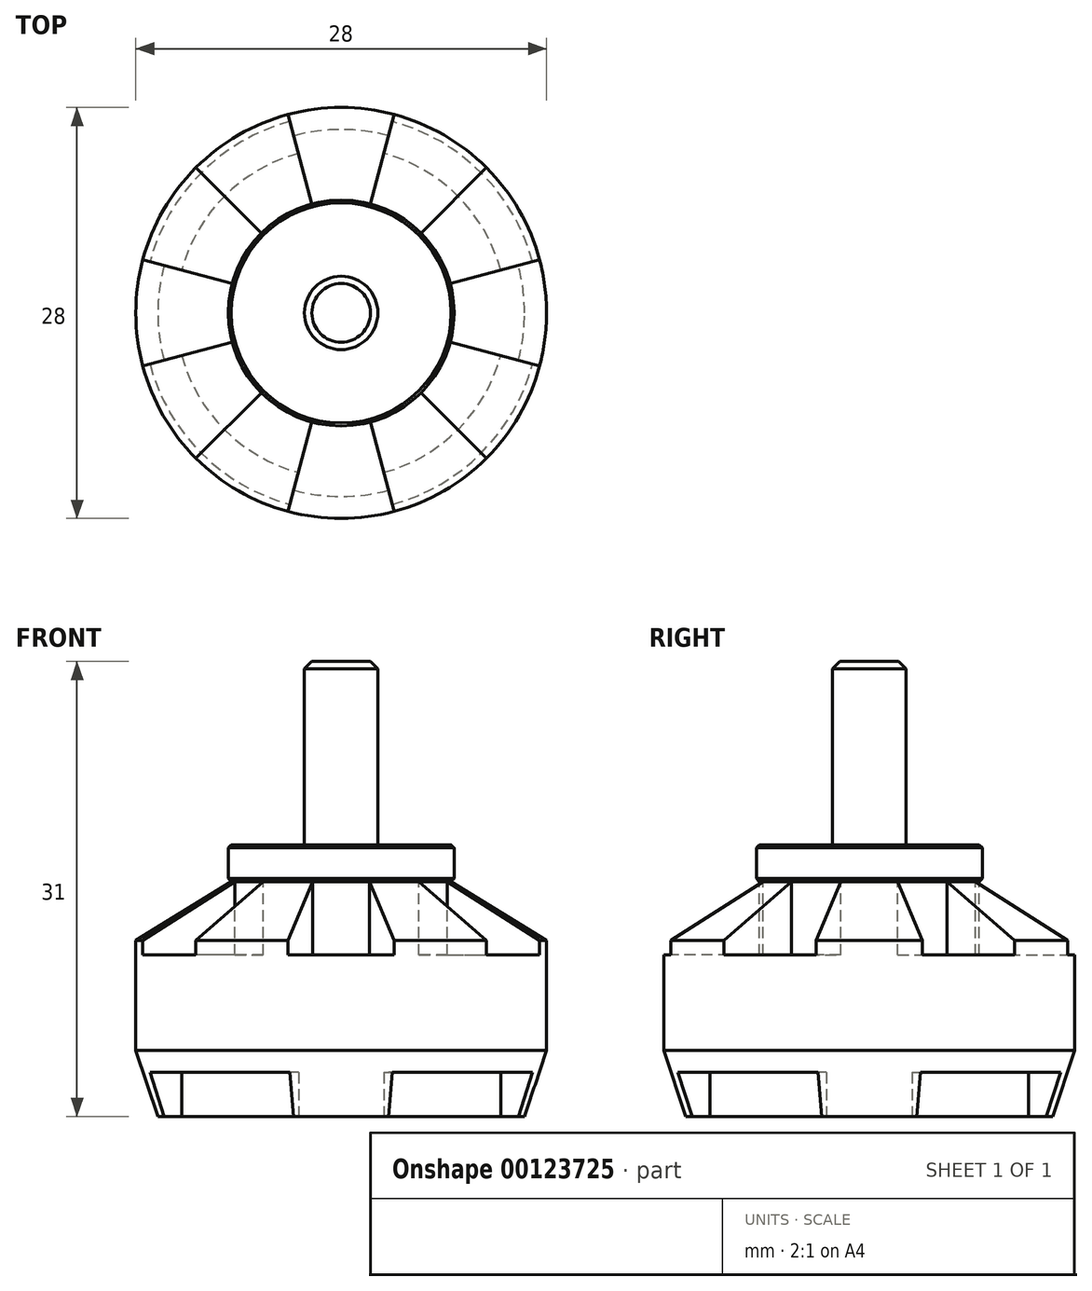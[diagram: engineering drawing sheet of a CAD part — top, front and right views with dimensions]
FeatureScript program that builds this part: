
annotation { "Feature Type Name" : "Feature", "Feature Type Description" : "" }
export const myFeature = defineFeature(function(context is Context, id is Id, definition is map)
    precondition{}
    {
        {
            var Q0;
            Q0=qCreatedBy(makeId("Front.planeOp"),FACE);
            var sketch = newSketch(context, id + "F0", { "sketchPlane" : qUnion([Q0])});
            skLineSegment(sketch, "E0.top", {"start": v(0, 0) * mm, "end": v(12.5, 0) * mm});
            skLineSegment(sketch, "E0.right", {"start": v(14, 12) * mm, "end": v(14, 4.5) * mm});
            skLineSegment(sketch, "E1", {"start": v(0, 16) * mm, "end": v(7.5, 16) * mm});
            skLineSegment(sketch, "E2", {"start": v(7.5, 16) * mm, "end": v(14, 12) * mm});
            skLineSegment(sketch, "E3", {"start": v(0, 16) * mm, "end": v(0, 0) * mm});
            skLineSegment(sketch, "E4", {"start": v(12.5, 0) * mm, "end": v(14, 4.5) * mm});
            skPoint(sketch, "E5.orphan", {"position": v(14, 0) * mm});
            skSolve(sketch);
        }
        {
            var Q0;
            Q0=qSketchRegion(id+"F0",true);
            var Q1;
            Q1=sQuery(id+"F0.wireOp",EDGE,"E3");
            revolve(context, id + "F1", {"entities" : qUnion([Q0]), "axis" : qUnion([Q1]), "revolveType" : RevolveType.FULL});
        }
        {
            var Q0;
            Q0=makeQuery(id+"F1.opRevolve","SWEPT_FACE",FACE,{"disambiguationData":[OSD([sQuery(id+"F0.wireOp",EDGE,"E1")])]});
            var sketch = newSketch(context, id + "F2", { "sketchPlane" : qUnion([Q0])});
            skArc(sketch, "E6", {"start": v(1.94, 7.24) * mm, "mid": v(0, 7.5) * mm, "end": v(-1.94, 7.24) * mm});
            skArc(sketch, "E7", {"start": v(3.62, 13.52) * mm, "mid": v(0, 14) * mm, "end": v(-3.62, 13.52) * mm});
            skLineSegment(sketch, "E8", {"start": v(0, 0) * mm, "end": v(-1.94, 7.24) * mm, "construction": true});
            skLineSegment(sketch, "E9", {"start": v(-1.94, 7.24) * mm, "end": v(-3.62, 13.52) * mm});
            skLineSegment(sketch, "E10", {"start": v(0, 0) * mm, "end": v(1.94, 7.24) * mm, "construction": true});
            skLineSegment(sketch, "E11", {"start": v(1.94, 7.24) * mm, "end": v(3.62, 13.52) * mm});
            skArc(sketch, "E12.1.0", {"start": v(-5.3, 5.3) * mm, "mid": v(-6.5, 3.75) * mm, "end": v(-7.24, 1.94) * mm});
            skArc(sketch, "E12.1.1", {"start": v(-9.9, 9.9) * mm, "mid": v(-12.12, 7) * mm, "end": v(-13.52, 3.62) * mm});
            skLineSegment(sketch, "E12.1.2", {"start": v(-5.3, 5.3) * mm, "end": v(-9.9, 9.9) * mm});
            skLineSegment(sketch, "E12.1.3", {"start": v(-7.24, 1.94) * mm, "end": v(-13.52, 3.62) * mm});
            skArc(sketch, "E12.2.0", {"start": v(-7.24, -1.94) * mm, "mid": v(-6.5, -3.75) * mm, "end": v(-5.3, -5.3) * mm});
            skArc(sketch, "E12.2.1", {"start": v(-13.52, -3.62) * mm, "mid": v(-12.12, -7) * mm, "end": v(-9.9, -9.9) * mm});
            skLineSegment(sketch, "E12.2.2", {"start": v(-7.24, -1.94) * mm, "end": v(-13.52, -3.62) * mm});
            skLineSegment(sketch, "E12.2.3", {"start": v(-5.3, -5.3) * mm, "end": v(-9.9, -9.9) * mm});
            skArc(sketch, "E12.3.0", {"start": v(-1.94, -7.24) * mm, "mid": v(0, -7.5) * mm, "end": v(1.94, -7.24) * mm});
            skArc(sketch, "E12.3.1", {"start": v(-3.62, -13.52) * mm, "mid": v(0, -14) * mm, "end": v(3.62, -13.52) * mm});
            skLineSegment(sketch, "E12.3.2", {"start": v(-1.94, -7.24) * mm, "end": v(-3.62, -13.52) * mm});
            skLineSegment(sketch, "E12.3.3", {"start": v(1.94, -7.24) * mm, "end": v(3.62, -13.52) * mm});
            skArc(sketch, "E12.4.0", {"start": v(5.3, -5.3) * mm, "mid": v(6.5, -3.75) * mm, "end": v(7.24, -1.94) * mm});
            skArc(sketch, "E12.4.1", {"start": v(9.9, -9.9) * mm, "mid": v(12.12, -7) * mm, "end": v(13.52, -3.62) * mm});
            skLineSegment(sketch, "E12.4.2", {"start": v(5.3, -5.3) * mm, "end": v(9.9, -9.9) * mm});
            skLineSegment(sketch, "E12.4.3", {"start": v(7.24, -1.94) * mm, "end": v(13.52, -3.62) * mm});
            skArc(sketch, "E12.5.0", {"start": v(7.24, 1.94) * mm, "mid": v(6.5, 3.75) * mm, "end": v(5.3, 5.3) * mm});
            skArc(sketch, "E12.5.1", {"start": v(13.52, 3.62) * mm, "mid": v(12.12, 7) * mm, "end": v(9.9, 9.9) * mm});
            skLineSegment(sketch, "E12.5.2", {"start": v(7.24, 1.94) * mm, "end": v(13.52, 3.62) * mm});
            skLineSegment(sketch, "E12.5.3", {"start": v(5.3, 5.3) * mm, "end": v(9.9, 9.9) * mm});
            skSolve(sketch);
        }
        {
            var Q0;
            Q0=qSketchRegion(id+"F2",true);
            extrude(context, id + "F3", {"entities" : qUnion([Q0]), "operationType" : NewBodyOperationType.REMOVE, "oppositeDirection" : true, "depth" : 5 * mm});
        }
        {
            var Q0;
            Q0=makeQuery(id+"F1.opRevolve","SWEPT_FACE",FACE,{"disambiguationData":[OSD([sQuery(id+"F0.wireOp",EDGE,"E0.top")])]});
            var sketch = newSketch(context, id + "F4", { "sketchPlane" : qUnion([Q0])});
            skArc(sketch, "E13", {"start": v(10.87, 2.91) * mm, "mid": v(7.95, 7.95) * mm, "end": v(2.91, 10.87) * mm});
            skArc(sketch, "E14", {"start": v(13.52, 3.62) * mm, "mid": v(9.9, 9.9) * mm, "end": v(3.62, 13.52) * mm});
            skLineSegment(sketch, "E15", {"start": v(0, 0) * mm, "end": v(2.91, 10.87) * mm, "construction": true});
            skLineSegment(sketch, "E16", {"start": v(2.91, 10.87) * mm, "end": v(3.62, 13.52) * mm});
            skLineSegment(sketch, "E17", {"start": v(0, 0) * mm, "end": v(10.87, 2.91) * mm, "construction": true});
            skLineSegment(sketch, "E18", {"start": v(10.87, 2.91) * mm, "end": v(13.52, 3.62) * mm});
            skArc(sketch, "E19.1.0", {"start": v(-3.62, 13.52) * mm, "mid": v(-9.9, 9.9) * mm, "end": v(-13.52, 3.62) * mm});
            skArc(sketch, "E19.1.1", {"start": v(-2.91, 10.87) * mm, "mid": v(-7.95, 7.95) * mm, "end": v(-10.87, 2.91) * mm});
            skLineSegment(sketch, "E19.1.2", {"start": v(-10.87, 2.91) * mm, "end": v(-13.52, 3.62) * mm});
            skLineSegment(sketch, "E19.1.3", {"start": v(-2.91, 10.87) * mm, "end": v(-3.62, 13.52) * mm});
            skArc(sketch, "E19.2.0", {"start": v(-13.52, -3.62) * mm, "mid": v(-9.9, -9.9) * mm, "end": v(-3.62, -13.52) * mm});
            skArc(sketch, "E19.2.1", {"start": v(-10.87, -2.91) * mm, "mid": v(-7.95, -7.95) * mm, "end": v(-2.91, -10.87) * mm});
            skLineSegment(sketch, "E19.2.2", {"start": v(-2.91, -10.87) * mm, "end": v(-3.62, -13.52) * mm});
            skLineSegment(sketch, "E19.2.3", {"start": v(-10.87, -2.91) * mm, "end": v(-13.52, -3.62) * mm});
            skArc(sketch, "E19.3.0", {"start": v(3.62, -13.52) * mm, "mid": v(9.9, -9.9) * mm, "end": v(13.52, -3.62) * mm});
            skArc(sketch, "E19.3.1", {"start": v(2.91, -10.87) * mm, "mid": v(7.95, -7.95) * mm, "end": v(10.87, -2.91) * mm});
            skLineSegment(sketch, "E19.3.2", {"start": v(10.87, -2.91) * mm, "end": v(13.52, -3.62) * mm});
            skLineSegment(sketch, "E19.3.3", {"start": v(2.91, -10.87) * mm, "end": v(3.62, -13.52) * mm});
            skLineSegment(sketch, "E20", {"start": v(0, 0) * mm, "end": v(-2.91, 10.87) * mm, "construction": true});
            skLineSegment(sketch, "E21", {"start": v(0, 0) * mm, "end": v(-10.87, 2.91) * mm, "construction": true});
            skLineSegment(sketch, "E22", {"start": v(0, 0) * mm, "end": v(-10.87, -2.91) * mm, "construction": true});
            skLineSegment(sketch, "E23", {"start": v(0, 0) * mm, "end": v(-2.91, -10.87) * mm, "construction": true});
            skLineSegment(sketch, "E24", {"start": v(0, 0) * mm, "end": v(2.91, -10.87) * mm, "construction": true});
            skLineSegment(sketch, "E25", {"start": v(0, 0) * mm, "end": v(10.87, -2.91) * mm, "construction": true});
            skSolve(sketch);
        }
        {
            var Q0;
            Q0=qSketchRegion(id+"F4",true);
            extrude(context, id + "F5", {"entities" : qUnion([Q0]), "operationType" : NewBodyOperationType.REMOVE, "oppositeDirection" : true, "depth" : 3 * mm});
        }
        {
            var Q0;
            Q0=qCreatedBy(makeId("Front.planeOp"),FACE);
            var sketch = newSketch(context, id + "F6", { "sketchPlane" : qUnion([Q0])});
            skLineSegment(sketch, "E26", {"start": v(0, 16) * mm, "end": v(7.5, 16) * mm});
            skLineSegment(sketch, "E27", {"start": v(7.7, 16.2) * mm, "end": v(7.7, 18.3) * mm});
            skLineSegment(sketch, "E28", {"start": v(7.5, 18.5) * mm, "end": v(2.5, 18.5) * mm});
            skLineSegment(sketch, "E29", {"start": v(2.5, 18.5) * mm, "end": v(2.5, 30.5) * mm});
            skLineSegment(sketch, "E30", {"start": v(2, 31) * mm, "end": v(0, 31) * mm});
            skLineSegment(sketch, "E31", {"start": v(0, 31) * mm, "end": v(0, 16) * mm});
            skLineSegment(sketch, "E32", {"start": v(7.5, 16) * mm, "end": v(7.7, 16.2) * mm});
            skLineSegment(sketch, "E33", {"start": v(7.5, 18.5) * mm, "end": v(7.7, 18.3) * mm});
            skPoint(sketch, "E34.orphan", {"position": v(7.7, 16) * mm});
            skLineSegment(sketch, "E35", {"start": v(2, 31) * mm, "end": v(2.5, 30.5) * mm});
            skSolve(sketch);
        }
        {
            var Q0;
            Q0=qSketchRegion(id+"F6",true);
            var Q1;
            Q1=sQuery(id+"F6.wireOp",EDGE,"E31");
            revolve(context, id + "F7", {"operationType" : NewBodyOperationType.ADD, "entities" : qUnion([Q0]), "axis" : qUnion([Q1]), "revolveType" : RevolveType.FULL});
        }
    });
